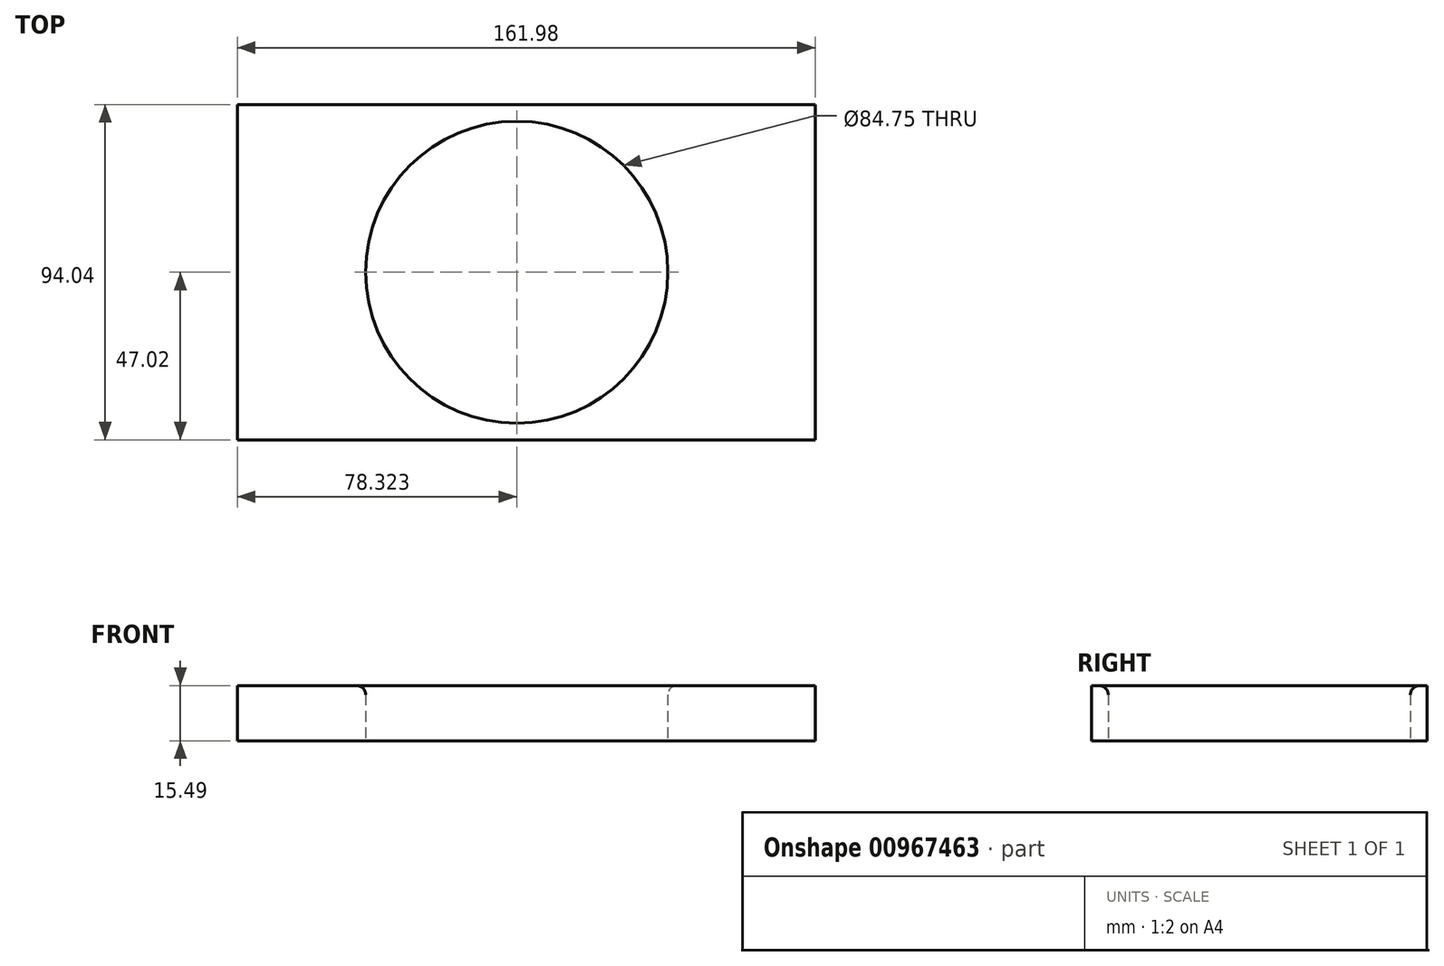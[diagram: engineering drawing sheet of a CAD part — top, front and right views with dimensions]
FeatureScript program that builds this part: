
annotation { "Feature Type Name" : "Feature", "Feature Type Description" : "" }
export const myFeature = defineFeature(function(context is Context, id is Id, definition is map)
    precondition{}
    {
        {
            var Q0;
            Q0=qCreatedBy(makeId("Top.planeOp"),FACE);
            var sketch = newSketch(context, id + "F0", { "sketchPlane" : qUnion([Q0])});
            skLineSegment(sketch, "E0.bottom", {"start": v(-81, 47.02) * mm, "end": v(81, 47.02) * mm});
            skLineSegment(sketch, "E0.top", {"start": v(-81, -47.02) * mm, "end": v(81, -47.02) * mm});
            skLineSegment(sketch, "E0.left", {"start": v(-81, 47.02) * mm, "end": v(-81, -47.02) * mm});
            skLineSegment(sketch, "E0.right", {"start": v(81, 47.02) * mm, "end": v(81, -47.02) * mm});
            skPoint(sketch, "E0.middle", {"position": v(0, 0) * mm});
            skCircle(sketch, "E1", {"center": v(-2.67, 0) * mm, "radius": 42.38 * mm});
            skSolve(sketch);
        }
        {
            var Q0;
            Q0=makeQuery(id+"F0.imprint","IMPRINT",FACE,{"disambiguationData":[TD([[makeQuery(id+"F0.imprint","IMPRINT",EDGE,{"derivedFrom":sQuery(id+"F0.wireOp",EDGE,"E0.bottom")}),-1.0]])]});
            extrude(context, id + "F1", {"entities" : qUnion([Q0]), "depth" : 15.5 * mm, "offsetDistance" : 25.4 * mm});
        }
        {
            var Q0;
            Q0=makeQuery(id+"F1.opExtrude","CAP_EDGE",EDGE,{"disambiguationData":[OSD([sQuery(id+"F0.wireOp",EDGE,"E1")])],"isStart":false});
            fillet(context, id + "F2", {"entities" : qUnion([Q0]), "radius" : 2.54 * mm, "tangentPropagation" : true, "allowEdgeOverflow" : false});
        }
    });
